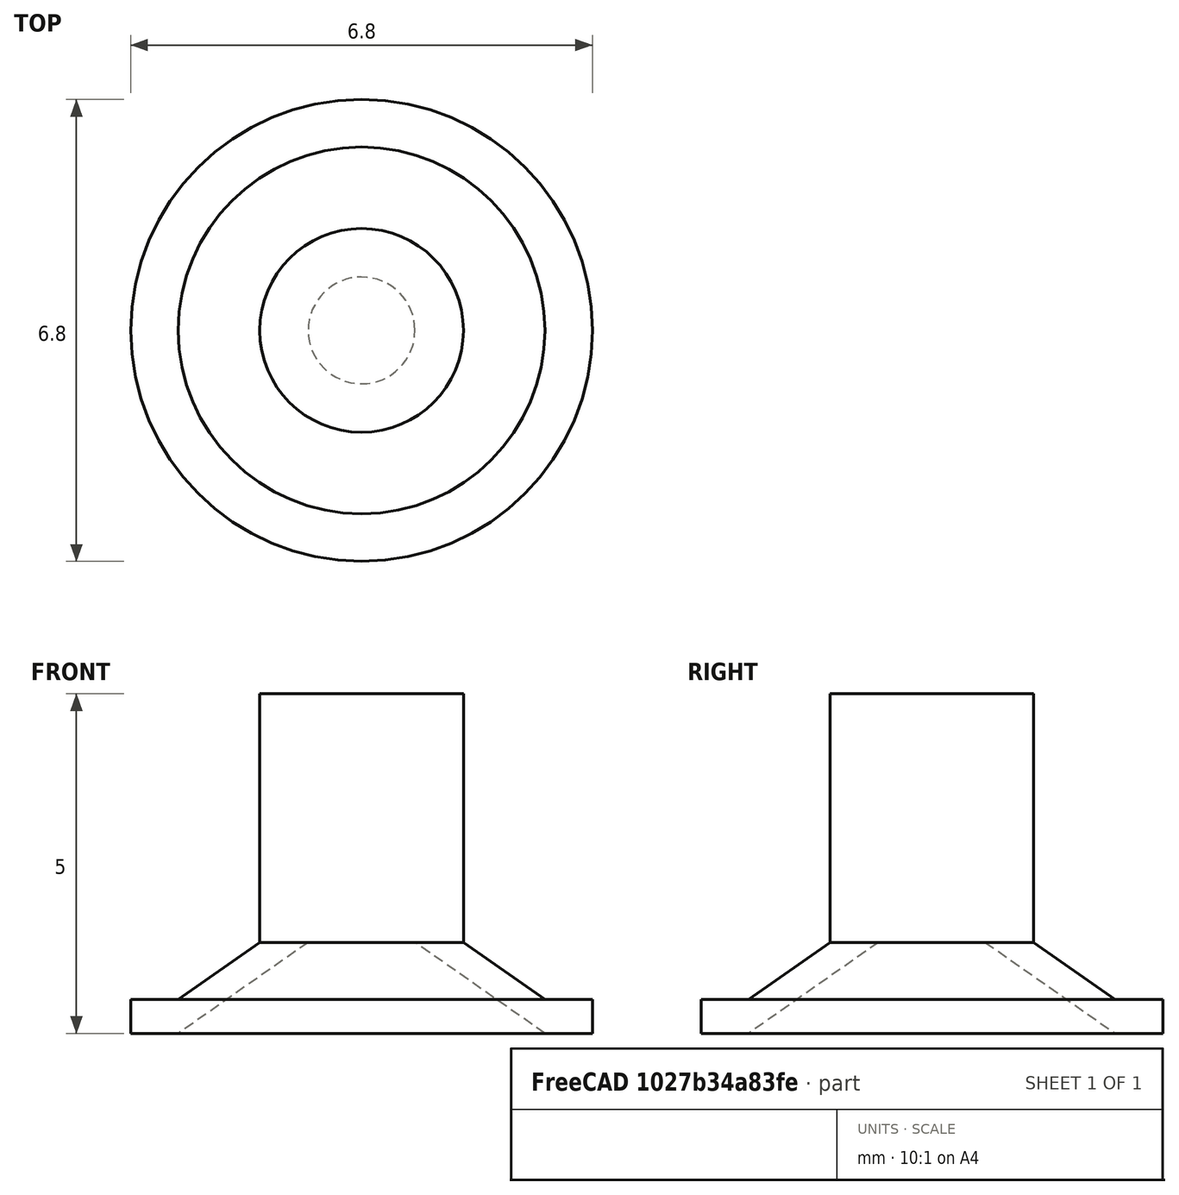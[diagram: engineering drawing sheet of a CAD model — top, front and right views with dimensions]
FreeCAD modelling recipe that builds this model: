
FCSTD DOCUMENT  (FreeCAD 0.19R24267 +99 (Git))
Label: button_v2
License: All rights reserved
LicenseURL: http://en.wikipedia.org/wiki/All_rights_reserved
objects: Sketcher::SketchObject×1, PartDesign::Revolution×1, PartDesign::Body×1
note: 4 computed .brp shape members not serialized (recipe doc carries the construction recipe); baked Part::Feature solids carry a one-line shape summary decoded from their .brp

FEATURE [Sketcher::SketchObject] Sketch
  FullyConstrained = true
  MapMode = 5
  Placement = pos=(0,0,0) rot=(1,0,0;1.5708rad)
  Support = -> [XZ_Plane]
  sketch-geometry (10):
    g0: LineSegment StartX=0 StartY=5 StartZ=0 EndX=1.5 EndY=5 EndZ=0
    g1: LineSegment StartX=1.5 StartY=5 StartZ=0 EndX=1.5 EndY=1.34025 EndZ=0
    g2: LineSegment StartX=1.5 StartY=1.34025 StartZ=0 EndX=2.7 EndY=0.5 EndZ=0
    g3: LineSegment StartX=2.7 StartY=0.5 StartZ=0 EndX=3.4 EndY=0.5 EndZ=0
    g4: LineSegment StartX=3.4 StartY=0.5 StartZ=0 EndX=3.4 EndY=0 EndZ=0
    g5: LineSegment StartX=3.4 StartY=0 StartZ=0 EndX=2.7 EndY=0 EndZ=0
    g6: LineSegment StartX=2.7 StartY=0 StartZ=0 EndX=0.785926 EndY=1.34025 EndZ=0
    g7: LineSegment StartX=0.785926 StartY=1.34025 StartZ=0 EndX=0 EndY=1.34025 EndZ=0
    g8: LineSegment StartX=0 StartY=1.34025 StartZ=0 EndX=0 EndY=5 EndZ=0
    g9: LineSegment StartX=0.785926 StartY=1.34025 StartZ=0 EndX=1.5 EndY=1.34025 EndZ=0
  constraints (29):
    c: PointOnObject(g0,g-2)
    c: Horizontal(g0)
    c: Coincident(g1,g0)
    c: Vertical(g1)
    c: Coincident(g2,g1)
    c: Coincident(g3,g2)
    c: Horizontal(g3)
    c: Coincident(g4,g3)
    c: PointOnObject(g4,g-1)
    c: Vertical(g4)
    c: Coincident(g5,g4)
    c: Horizontal(g5)
    c: Coincident(g6,g5)
    c: Coincident(g7,g6)
    c: Horizontal(g7)
    c: Coincident(g8,g7)
    c: Coincident(g8,g0)
    c: Vertical(g8)
    c: Parallel(g6,g2)
    c: DistanceX(g0,g0) = 1.5
    c: DistanceX(g-1,g4) = 3.4
    c: Coincident(g9,g6)
    c: Coincident(g9,g1)
    c: Horizontal(g9)
    c: Angle(g5,g6) = 2.53073
    c: DistanceY(g4,g4) = 0.5
    c: DistanceX(g3,g3) = 0.7
    c: DistanceY(g-1,g0) = 5
    c: DistanceX(g5,g5) = 0.7
FEATURE [PartDesign::Revolution] Revolution
  Angle = 360
  Axis = (0,-2e-16,1)
  Base = (0,0,0)
  Placement = pos=(0,0,0) rot=(1,0,0;1.5708rad)
  Profile = -> Sketch
  ReferenceAxis = -> Sketch [V_Axis]
  Reversed = true
FEATURE [PartDesign::Body] Body
  Group = -> [Sketch,Revolution]
  Origin = -> Origin
  Tip = -> Revolution
